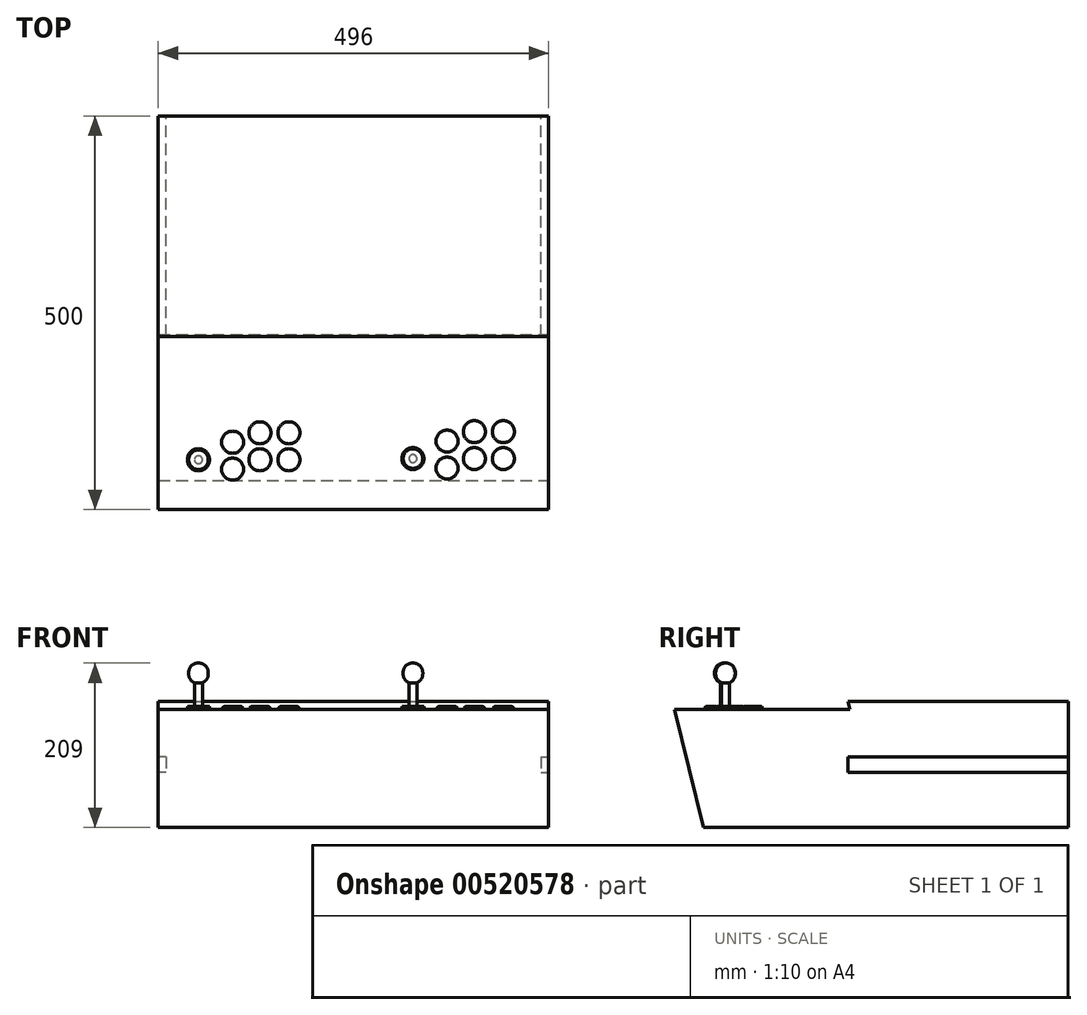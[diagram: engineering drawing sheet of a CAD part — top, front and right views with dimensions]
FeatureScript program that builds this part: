
annotation { "Feature Type Name" : "Feature", "Feature Type Description" : "" }
export const myFeature = defineFeature(function(context is Context, id is Id, definition is map)
    precondition{}
    {
        {
            var Q0;
            Q0=qCreatedBy(makeId("Front.planeOp"),FACE);
            var sketch = newSketch(context, id + "F0", { "sketchPlane" : qUnion([Q0])});
            skLineSegment(sketch, "E0.bottom", {"start": v(-79.05, 153.55) * mm, "end": v(420.95, 153.55) * mm});
            skLineSegment(sketch, "E0.top", {"start": v(-79.05, 3.55) * mm, "end": v(420.95, 3.55) * mm});
            skLineSegment(sketch, "E0.left", {"start": v(-79.05, 153.55) * mm, "end": v(-79.05, 3.55) * mm});
            skLineSegment(sketch, "E0.right", {"start": v(420.95, 153.55) * mm, "end": v(420.95, 3.55) * mm});
            skSolve(sketch);
        }
        {
            var Q0;
            Q0=makeQuery(id+"F0.imprint","IMPRINT",FACE,{"disambiguationData":[TD([[makeQuery(id+"F0.imprint","IMPRINT",EDGE,{"derivedFrom":sQuery(id+"F0.wireOp",EDGE,"E0.bottom")}),-1.0]])]});
            extrude(context, id + "F1", {"entities" : qUnion([Q0]), "depth" : 500 * mm, "offsetDistance" : 25 * mm});
        }
        {
            var Q0;
            Q0=makeQuery(id+"F1.opExtrude","SWEPT_FACE",FACE,{"disambiguationData":[OSD([sQuery(id+"F0.wireOp",EDGE,"E0.right")])]});
            var sketch = newSketch(context, id + "F2", { "sketchPlane" : qUnion([Q0])});
            skLineSegment(sketch, "E1", {"start": v(-500, 153.55) * mm, "end": v(-463.33, 3.55) * mm});
            skSolve(sketch);
        }
        {
            var Q0;
            {var subQ0=sQuery(id+"F2.wireOp",EDGE,"E1");Q0=makeQuery(id+"F2.imprint","IMPRINT",FACE,{"disambiguationData":[TD([[makeQuery(id+"F2.imprint","IMPRINT",EDGE,{"derivedFrom":subQ0}),-1.0]])]});}
            extrude(context, id + "F3", {"entities" : qUnion([Q0]), "operationType" : NewBodyOperationType.REMOVE, "oppositeDirection" : true, "depth" : 546 * mm, "offsetDistance" : 25 * mm});
        }
        {
            var Q0;
            Q0=makeQuery(id+"F1.opExtrude","SWEPT_FACE",FACE,{"disambiguationData":[OSD([sQuery(id+"F0.wireOp",EDGE,"E0.bottom")])]});
            var sketch = newSketch(context, id + "F4", { "sketchPlane" : qUnion([Q0])});
            skLineSegment(sketch, "E2", {"start": v(-79.05, -500) * mm, "end": v(-79.05, -280) * mm});
            skLineSegment(sketch, "E3", {"start": v(-79.05, -280) * mm, "end": v(420.95, -280) * mm});
            skSolve(sketch);
        }
        {
            var Q0;
            {var subQ0=sQuery(id+"F4.wireOp",EDGE,"E3");Q0=makeQuery(id+"F4.imprint","IMPRINT",FACE,{"disambiguationData":[TD([[makeQuery(id+"F4.imprint","IMPRINT",EDGE,{"derivedFrom":subQ0}),1.0]])]});}
            extrude(context, id + "F5", {"entities" : qUnion([Q0]), "operationType" : NewBodyOperationType.ADD, "depth" : 10 * mm, "offsetDistance" : 25 * mm});
        }
        {
            var Q0;
            {var subQ0=sQuery(id+"F0.wireOp",EDGE,"E0.right");Q0=makeQuery(id+"F5.boolean.opBoolean","MERGE",FACE,{"derivedFrom":[makeQuery(id+"F1.opExtrude","SWEPT_FACE",FACE,{"disambiguationData":[OSD([subQ0])]}),makeQuery(id+"F5.opExtrude","SWEPT_FACE",FACE,{"disambiguationData":[OSD([sQuery(id+"F0.wireOp",EDGE,"E0.bottom"),subQ0])]})]});}
            extrude(context, id + "F6", {"entities" : qUnion([Q0]), "operationType" : NewBodyOperationType.REMOVE, "oppositeDirection" : true, "depth" : 2 * mm, "offsetDistance" : 25 * mm});
        }
        {
            var Q0;
            {var subQ0=sQuery(id+"F0.wireOp",EDGE,"E0.left");Q0=makeQuery(id+"F5.boolean.opBoolean","MERGE",FACE,{"derivedFrom":[makeQuery(id+"F1.opExtrude","SWEPT_FACE",FACE,{"disambiguationData":[OSD([subQ0])]}),makeQuery(id+"F5.opExtrude","SWEPT_FACE",FACE,{"disambiguationData":[OSD([sQuery(id+"F0.wireOp",EDGE,"E0.bottom"),subQ0])]})]});}
            extrude(context, id + "F7", {"entities" : qUnion([Q0]), "operationType" : NewBodyOperationType.REMOVE, "oppositeDirection" : true, "depth" : 2 * mm, "offsetDistance" : 25 * mm});
        }
        {
            var Q0;
            Q0=makeQuery(id+"F7.boolean.opBoolean","COPY",FACE,{"derivedFrom":makeQuery(id+"F7.opExtrude","CAP_FACE",FACE,{"disambiguationData":[OSD([sQuery(id+"F0.wireOp",EDGE,"E0.bottom"),sQuery(id+"F0.wireOp",EDGE,"E0.left")])],"isStart":false})});
            var sketch = newSketch(context, id + "F8", { "sketchPlane" : qUnion([Q0])});
            skLineSegment(sketch, "E4", {"start": v(0, 3.55) * mm, "end": v(0, 83.55) * mm});
            skLineSegment(sketch, "E5", {"start": v(0, 83.55) * mm, "end": v(280, 83.55) * mm});
            skLineSegment(sketch, "E6", {"start": v(280, 83.55) * mm, "end": v(280, 93.55) * mm});
            skLineSegment(sketch, "E7", {"start": v(280, 83.55) * mm, "end": v(280, 73.55) * mm});
            skLineSegment(sketch, "E8", {"start": v(280, 93.55) * mm, "end": v(0, 93.55) * mm});
            skLineSegment(sketch, "E9", {"start": v(280, 73.55) * mm, "end": v(0, 73.55) * mm});
            skSolve(sketch);
        }
        {
            var Q0;
            {var subQ0=sQuery(id+"F8.wireOp",EDGE,"E5");Q0=makeQuery(id+"F8.imprint","IMPRINT",FACE,{"disambiguationData":[TD([[makeQuery(id+"F8.imprint","IMPRINT",EDGE,{"derivedFrom":subQ0}),1.0]])]});}
            var Q1;
            {var subQ0=sQuery(id+"F8.wireOp",EDGE,"E5");Q1=makeQuery(id+"F8.imprint","IMPRINT",FACE,{"disambiguationData":[TD([[makeQuery(id+"F8.imprint","IMPRINT",EDGE,{"derivedFrom":subQ0}),-1.0]])]});}
            extrude(context, id + "F9", {"entities" : qUnion([Q0, Q1]), "operationType" : NewBodyOperationType.REMOVE, "oppositeDirection" : true, "depth" : 10 * mm, "offsetDistance" : 25 * mm});
        }
        {
            var Q0;
            Q0=makeQuery(id+"F6.boolean.opBoolean","COPY",FACE,{"derivedFrom":makeQuery(id+"F6.opExtrude","CAP_FACE",FACE,{"disambiguationData":[OSD([sQuery(id+"F0.wireOp",EDGE,"E0.bottom"),sQuery(id+"F0.wireOp",EDGE,"E0.right")])],"isStart":false})});
            var sketch = newSketch(context, id + "F10", { "sketchPlane" : qUnion([Q0])});
            skLineSegment(sketch, "E10", {"start": v(0, 3.55) * mm, "end": v(0, 83.55) * mm});
            skLineSegment(sketch, "E11", {"start": v(0, 83.55) * mm, "end": v(-280, 83.55) * mm});
            skLineSegment(sketch, "E12", {"start": v(-280, 83.55) * mm, "end": v(-280, 93.55) * mm});
            skLineSegment(sketch, "E13", {"start": v(-280, 93.55) * mm, "end": v(-280, 83.55) * mm});
            skLineSegment(sketch, "E14", {"start": v(-280, 83.55) * mm, "end": v(-280, 73.55) * mm});
            skLineSegment(sketch, "E15.bottom", {"start": v(-280, 93.55) * mm, "end": v(-280, 93.55) * mm});
            skLineSegment(sketch, "E15.top", {"start": v(-280, 73.55) * mm, "end": v(-280, 73.55) * mm});
            skLineSegment(sketch, "E15.left", {"start": v(-280, 93.55) * mm, "end": v(-280, 73.55) * mm});
            skLineSegment(sketch, "E15.right", {"start": v(-280, 93.55) * mm, "end": v(-280, 73.55) * mm});
            skLineSegment(sketch, "E16.bottom", {"start": v(-280, 73.55) * mm, "end": v(0, 73.55) * mm});
            skLineSegment(sketch, "E16.top", {"start": v(-280, 93.55) * mm, "end": v(0, 93.55) * mm});
            skLineSegment(sketch, "E16.left", {"start": v(-280, 73.55) * mm, "end": v(-280, 93.55) * mm});
            skLineSegment(sketch, "E16.right", {"start": v(0, 73.55) * mm, "end": v(0, 93.55) * mm});
            skSolve(sketch);
        }
        {
            var Q0;
            {var subQ0=sQuery(id+"F10.wireOp",EDGE,"E11");Q0=makeQuery(id+"F10.imprint","IMPRINT",FACE,{"disambiguationData":[TD([[makeQuery(id+"F10.imprint","IMPRINT",EDGE,{"derivedFrom":subQ0}),1.0]])]});}
            var Q1;
            {var subQ0=sQuery(id+"F10.wireOp",EDGE,"E11");Q1=makeQuery(id+"F10.imprint","IMPRINT",FACE,{"disambiguationData":[TD([[makeQuery(id+"F10.imprint","IMPRINT",EDGE,{"derivedFrom":subQ0}),-1.0]])]});}
            extrude(context, id + "F11", {"entities" : qUnion([Q0, Q1]), "operationType" : NewBodyOperationType.REMOVE, "oppositeDirection" : true, "depth" : 10 * mm, "offsetDistance" : 25 * mm});
        }
        {
            var Q0;
            Q0=makeQuery(id+"F1.opExtrude","SWEPT_FACE",FACE,{"disambiguationData":[OSD([sQuery(id+"F0.wireOp",EDGE,"E0.bottom")])]});
            var sketch = newSketch(context, id + "F12", { "sketchPlane" : qUnion([Q0])});
            skCircle(sketch, "E17", {"center": v(-25.85, -436.75) * mm, "radius": 14 * mm});
            skCircle(sketch, "E18", {"center": v(17.5, -414.5) * mm, "radius": 14 * mm});
            skCircle(sketch, "E19", {"center": v(17.5, -448.75) * mm, "radius": 14 * mm});
            skCircle(sketch, "E20", {"center": v(52.2, -402.5) * mm, "radius": 14 * mm});
            skCircle(sketch, "E21", {"center": v(52.2, -436.75) * mm, "radius": 14 * mm});
            skCircle(sketch, "E22", {"center": v(89, -402.5) * mm, "radius": 14 * mm});
            skCircle(sketch, "E23", {"center": v(89, -436.75) * mm, "radius": 14 * mm});
            skCircle(sketch, "E24", {"center": v(246.58, -435.28) * mm, "radius": 14 * mm});
            skCircle(sketch, "E25", {"center": v(289.91, -413.04) * mm, "radius": 14 * mm});
            skCircle(sketch, "E26", {"center": v(289.91, -447.28) * mm, "radius": 14 * mm});
            skCircle(sketch, "E27", {"center": v(324.63, -401.04) * mm, "radius": 14 * mm});
            skCircle(sketch, "E28", {"center": v(324.63, -435.28) * mm, "radius": 14 * mm});
            skCircle(sketch, "E29", {"center": v(361.43, -401.04) * mm, "radius": 14 * mm});
            skCircle(sketch, "E30", {"center": v(361.43, -435.28) * mm, "radius": 14 * mm});
            skSolve(sketch);
        }
        {
            var Q0;
            Q0=makeQuery(id+"F12.imprint","IMPRINT",FACE,{"disambiguationData":[TD([[makeQuery(id+"F12.imprint","IMPRINT",EDGE,{"derivedFrom":sQuery(id+"F12.wireOp",EDGE,"E17")}),1.0]])]});
            var Q1;
            Q1=makeQuery(id+"F12.imprint","IMPRINT",FACE,{"disambiguationData":[TD([[makeQuery(id+"F12.imprint","IMPRINT",EDGE,{"derivedFrom":sQuery(id+"F12.wireOp",EDGE,"E19")}),1.0]])]});
            var Q2;
            Q2=makeQuery(id+"F12.imprint","IMPRINT",FACE,{"disambiguationData":[TD([[makeQuery(id+"F12.imprint","IMPRINT",EDGE,{"derivedFrom":sQuery(id+"F12.wireOp",EDGE,"E21")}),1.0]])]});
            var Q3;
            Q3=makeQuery(id+"F12.imprint","IMPRINT",FACE,{"disambiguationData":[TD([[makeQuery(id+"F12.imprint","IMPRINT",EDGE,{"derivedFrom":sQuery(id+"F12.wireOp",EDGE,"E23")}),1.0]])]});
            var Q4;
            Q4=makeQuery(id+"F12.imprint","IMPRINT",FACE,{"disambiguationData":[TD([[makeQuery(id+"F12.imprint","IMPRINT",EDGE,{"derivedFrom":sQuery(id+"F12.wireOp",EDGE,"E22")}),1.0]])]});
            var Q5;
            Q5=makeQuery(id+"F12.imprint","IMPRINT",FACE,{"disambiguationData":[TD([[makeQuery(id+"F12.imprint","IMPRINT",EDGE,{"derivedFrom":sQuery(id+"F12.wireOp",EDGE,"E20")}),1.0]])]});
            var Q6;
            Q6=makeQuery(id+"F12.imprint","IMPRINT",FACE,{"disambiguationData":[TD([[makeQuery(id+"F12.imprint","IMPRINT",EDGE,{"derivedFrom":sQuery(id+"F12.wireOp",EDGE,"E18")}),1.0]])]});
            var Q7;
            Q7=makeQuery(id+"F12.imprint","IMPRINT",FACE,{"disambiguationData":[TD([[makeQuery(id+"F12.imprint","IMPRINT",EDGE,{"derivedFrom":sQuery(id+"F12.wireOp",EDGE,"E24")}),1.0]])]});
            var Q8;
            Q8=makeQuery(id+"F12.imprint","IMPRINT",FACE,{"disambiguationData":[TD([[makeQuery(id+"F12.imprint","IMPRINT",EDGE,{"derivedFrom":sQuery(id+"F12.wireOp",EDGE,"E26")}),1.0]])]});
            var Q9;
            Q9=makeQuery(id+"F12.imprint","IMPRINT",FACE,{"disambiguationData":[TD([[makeQuery(id+"F12.imprint","IMPRINT",EDGE,{"derivedFrom":sQuery(id+"F12.wireOp",EDGE,"E25")}),1.0]])]});
            var Q10;
            Q10=makeQuery(id+"F12.imprint","IMPRINT",FACE,{"disambiguationData":[TD([[makeQuery(id+"F12.imprint","IMPRINT",EDGE,{"derivedFrom":sQuery(id+"F12.wireOp",EDGE,"E28")}),1.0]])]});
            var Q11;
            Q11=makeQuery(id+"F12.imprint","IMPRINT",FACE,{"disambiguationData":[TD([[makeQuery(id+"F12.imprint","IMPRINT",EDGE,{"derivedFrom":sQuery(id+"F12.wireOp",EDGE,"E27")}),1.0]])]});
            var Q12;
            Q12=makeQuery(id+"F12.imprint","IMPRINT",FACE,{"disambiguationData":[TD([[makeQuery(id+"F12.imprint","IMPRINT",EDGE,{"derivedFrom":sQuery(id+"F12.wireOp",EDGE,"E29")}),1.0]])]});
            var Q13;
            Q13=makeQuery(id+"F12.imprint","IMPRINT",FACE,{"disambiguationData":[TD([[makeQuery(id+"F12.imprint","IMPRINT",EDGE,{"derivedFrom":sQuery(id+"F12.wireOp",EDGE,"E30")}),1.0]])]});
            extrude(context, id + "F13", {"entities" : qUnion([Q0, Q1, Q2, Q3, Q4, Q5, Q6, Q7, Q8, Q9, Q10, Q11, Q12, Q13]), "operationType" : NewBodyOperationType.ADD, "depth" : 4 * mm, "offsetDistance" : 25 * mm});
        }
        {
            var Q0;
            Q0=makeQuery(id+"F13.opExtrude","CAP_EDGE",EDGE,{"disambiguationData":[OSD([sQuery(id+"F12.wireOp",EDGE,"E19")])],"isStart":false});
            var Q1;
            Q1=makeQuery(id+"F13.opExtrude","CAP_EDGE",EDGE,{"disambiguationData":[OSD([sQuery(id+"F12.wireOp",EDGE,"E18")])],"isStart":false});
            var Q2;
            Q2=makeQuery(id+"F13.opExtrude","CAP_EDGE",EDGE,{"disambiguationData":[OSD([sQuery(id+"F12.wireOp",EDGE,"E20")])],"isStart":false});
            var Q3;
            Q3=makeQuery(id+"F13.opExtrude","CAP_EDGE",EDGE,{"disambiguationData":[OSD([sQuery(id+"F12.wireOp",EDGE,"E21")])],"isStart":false});
            var Q4;
            Q4=makeQuery(id+"F13.opExtrude","CAP_EDGE",EDGE,{"disambiguationData":[OSD([sQuery(id+"F12.wireOp",EDGE,"E23")])],"isStart":false});
            var Q5;
            Q5=makeQuery(id+"F13.opExtrude","CAP_EDGE",EDGE,{"disambiguationData":[OSD([sQuery(id+"F12.wireOp",EDGE,"E22")])],"isStart":false});
            var Q6;
            Q6=makeQuery(id+"F13.opExtrude","CAP_EDGE",EDGE,{"disambiguationData":[OSD([sQuery(id+"F12.wireOp",EDGE,"E26")])],"isStart":false});
            var Q7;
            Q7=makeQuery(id+"F13.opExtrude","CAP_EDGE",EDGE,{"disambiguationData":[OSD([sQuery(id+"F12.wireOp",EDGE,"E25")])],"isStart":false});
            var Q8;
            Q8=makeQuery(id+"F13.opExtrude","CAP_EDGE",EDGE,{"disambiguationData":[OSD([sQuery(id+"F12.wireOp",EDGE,"E27")])],"isStart":false});
            var Q9;
            Q9=makeQuery(id+"F13.opExtrude","CAP_EDGE",EDGE,{"disambiguationData":[OSD([sQuery(id+"F12.wireOp",EDGE,"E28")])],"isStart":false});
            var Q10;
            Q10=makeQuery(id+"F13.opExtrude","CAP_EDGE",EDGE,{"disambiguationData":[OSD([sQuery(id+"F12.wireOp",EDGE,"E30")])],"isStart":false});
            var Q11;
            Q11=makeQuery(id+"F13.opExtrude","CAP_EDGE",EDGE,{"disambiguationData":[OSD([sQuery(id+"F12.wireOp",EDGE,"E29")])],"isStart":false});
            fillet(context, id + "F14", {"entities" : qUnion([Q0, Q1, Q2, Q3, Q4, Q5, Q6, Q7, Q8, Q9, Q10, Q11]), "radius" : 5 * mm, "tangentPropagation" : true, "allowEdgeOverflow" : false});
        }
        {
            var Q0;
            Q0=makeQuery(id+"F13.opExtrude","CAP_FACE",FACE,{"disambiguationData":[OSD([sQuery(id+"F12.wireOp",EDGE,"E17")])],"isStart":false});
            var sketch = newSketch(context, id + "F15", { "sketchPlane" : qUnion([Q0])});
            skCircle(sketch, "E31", {"center": v(-25.85, -436.75) * mm, "radius": 5 * mm});
            skSolve(sketch);
        }
        {
            var Q0;
            Q0=makeQuery(id+"F15.imprint","IMPRINT",FACE,{"disambiguationData":[TD([[makeQuery(id+"F15.imprint","IMPRINT",EDGE,{"derivedFrom":sQuery(id+"F15.wireOp",EDGE,"E31")}),1.0]])]});
            extrude(context, id + "F16", {"entities" : qUnion([Q0]), "operationType" : NewBodyOperationType.ADD, "depth" : 30 * mm, "offsetDistance" : 25 * mm});
        }
        {
            var Q0;
            Q0=makeQuery(id+"F13.opExtrude","CAP_FACE",FACE,{"disambiguationData":[OSD([sQuery(id+"F12.wireOp",EDGE,"E24")])],"isStart":false});
            var sketch = newSketch(context, id + "F17", { "sketchPlane" : qUnion([Q0])});
            skCircle(sketch, "E32", {"center": v(246.58, -435.28) * mm, "radius": 5 * mm});
            skSolve(sketch);
        }
        {
            var Q0;
            Q0=makeQuery(id+"F17.imprint","IMPRINT",FACE,{"disambiguationData":[TD([[makeQuery(id+"F17.imprint","IMPRINT",EDGE,{"derivedFrom":sQuery(id+"F17.wireOp",EDGE,"E32")}),1.0]])]});
            extrude(context, id + "F18", {"entities" : qUnion([Q0]), "operationType" : NewBodyOperationType.ADD, "depth" : 30 * mm, "offsetDistance" : 25 * mm});
        }
        {
            var Q0;
            Q0=makeQuery(id+"F16.opExtrude","CAP_FACE",FACE,{"disambiguationData":[OSD([sQuery(id+"F15.wireOp",EDGE,"E31")])],"isStart":false});
            var sketch = newSketch(context, id + "F19", { "sketchPlane" : qUnion([Q0])});
            skCircle(sketch, "E33", {"center": v(-25.85, -436.75) * mm, "radius": 12.5 * mm});
            skSolve(sketch);
        }
        {
            var Q0;
            Q0=makeQuery(id+"F19.imprint","IMPRINT",FACE,{"disambiguationData":[TD([[makeQuery(id+"F19.imprint","IMPRINT",EDGE,{"derivedFrom":makeQuery(id+"F16.opExtrude","CAP_EDGE",EDGE,{"disambiguationData":[OSD([sQuery(id+"F15.wireOp",EDGE,"E31")])],"isStart":false})}),1.0]])]});
            var Q1;
            Q1=makeQuery(id+"F19.imprint","IMPRINT",FACE,{"disambiguationData":[TD([[makeQuery(id+"F19.imprint","IMPRINT",EDGE,{"derivedFrom":sQuery(id+"F19.wireOp",EDGE,"E33")}),1.0]])]});
            extrude(context, id + "F20", {"entities" : qUnion([Q0, Q1]), "operationType" : NewBodyOperationType.ADD, "depth" : 25 * mm, "offsetDistance" : 25 * mm});
        }
        {
            var Q0;
            Q0=makeQuery(id+"F20.opExtrude","CAP_EDGE",EDGE,{"disambiguationData":[OSD([sQuery(id+"F19.wireOp",EDGE,"E33")])],"isStart":false});
            var Q1;
            Q1=makeQuery(id+"F20.opExtrude","CAP_EDGE",EDGE,{"disambiguationData":[OSD([sQuery(id+"F19.wireOp",EDGE,"E33")])],"isStart":true});
            fillet(context, id + "F21", {"entities" : qUnion([Q0, Q1]), "radius" : 12 * mm, "tangentPropagation" : true, "allowEdgeOverflow" : false});
        }
        {
            var Q0;
            Q0=makeQuery(id+"F18.opExtrude","CAP_FACE",FACE,{"disambiguationData":[OSD([sQuery(id+"F17.wireOp",EDGE,"E32")])],"isStart":false});
            var sketch = newSketch(context, id + "F22", { "sketchPlane" : qUnion([Q0])});
            skCircle(sketch, "E34", {"center": v(246.58, -435.28) * mm, "radius": 12.5 * mm});
            skSolve(sketch);
        }
        {
            var Q0;
            Q0=makeQuery(id+"F22.imprint","IMPRINT",FACE,{"disambiguationData":[TD([[makeQuery(id+"F22.imprint","IMPRINT",EDGE,{"derivedFrom":makeQuery(id+"F18.opExtrude","CAP_EDGE",EDGE,{"disambiguationData":[OSD([sQuery(id+"F17.wireOp",EDGE,"E32")])],"isStart":false})}),1.0]])]});
            var Q1;
            Q1=makeQuery(id+"F22.imprint","IMPRINT",FACE,{"disambiguationData":[TD([[makeQuery(id+"F22.imprint","IMPRINT",EDGE,{"derivedFrom":sQuery(id+"F22.wireOp",EDGE,"E34")}),1.0]])]});
            extrude(context, id + "F23", {"entities" : qUnion([Q0, Q1]), "operationType" : NewBodyOperationType.ADD, "depth" : 25 * mm, "offsetDistance" : 25 * mm});
        }
        {
            var Q0;
            Q0=makeQuery(id+"F23.opExtrude","CAP_EDGE",EDGE,{"disambiguationData":[OSD([sQuery(id+"F22.wireOp",EDGE,"E34")])],"isStart":false});
            var Q1;
            Q1=makeQuery(id+"F23.opExtrude","CAP_EDGE",EDGE,{"disambiguationData":[OSD([sQuery(id+"F22.wireOp",EDGE,"E34")])],"isStart":true});
            fillet(context, id + "F24", {"entities" : qUnion([Q0, Q1]), "radius" : 12 * mm, "tangentPropagation" : true, "allowEdgeOverflow" : false});
        }
        {
            var Q0;
            Q0=makeQuery(id+"F6.boolean.opBoolean","COPY",FACE,{"derivedFrom":makeQuery(id+"F6.opExtrude","CAP_FACE",FACE,{"disambiguationData":[OSD([sQuery(id+"F0.wireOp",EDGE,"E0.bottom"),sQuery(id+"F0.wireOp",EDGE,"E0.right")])],"isStart":false})});
            var sketch = newSketch(context, id + "F25", { "sketchPlane" : qUnion([Q0])});
            skLineSegment(sketch, "E35", {"start": v(-280, 163.55) * mm, "end": v(-277.56, 153.55) * mm});
            skLineSegment(sketch, "E36", {"start": v(-280, 153.55) * mm, "end": v(-277.56, 153.55) * mm});
            skSolve(sketch);
        }
        {
            var Q0;
            Q0=makeQuery(id+"F25.imprint","IMPRINT",FACE,{"disambiguationData":[TD([[makeQuery(id+"F25.imprint","IMPRINT",EDGE,{"derivedFrom":sQuery(id+"F25.wireOp",EDGE,"E35")}),-1.0]])]});
            extrude(context, id + "F26", {"entities" : qUnion([Q0]), "operationType" : NewBodyOperationType.REMOVE, "endBound" : BoundingType.THROUGH_ALL, "oppositeDirection" : true, "depth" : 25 * mm, "offsetDistance" : 25 * mm});
        }
    });
